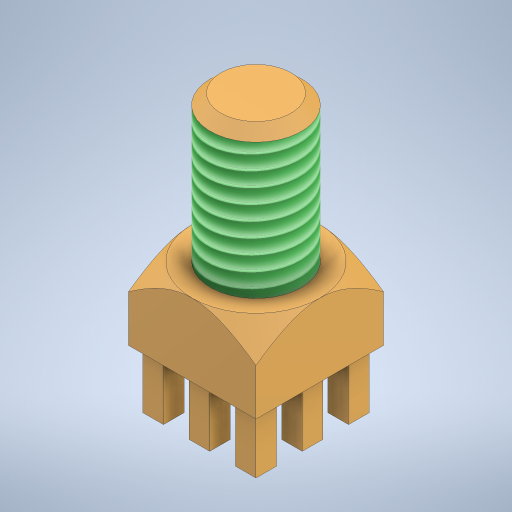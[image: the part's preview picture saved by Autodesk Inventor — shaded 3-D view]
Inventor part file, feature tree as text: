
AUTODESK INVENTOR PART (.ipt)
format: ipt  version: 2024 (Build 280153000, 153)  size: 371,712 bytes
history: native  units: mm
features: thread x1
ambient origin geometry x8: Origin, YZ Plane, XZ Plane, XY Plane, X Axis, Y Axis, Z Axis, Center Point
bodies: Volumenkörper1 (feature_tree)
feature tree (1):
  thread  "Gewinde1"  [1 undecoded]
note: 1 required parameter value undecoded (feature->parameter linkage not recoverable at this tier; creation-order binding heuristic only, values carry confidence <= 0.55)
